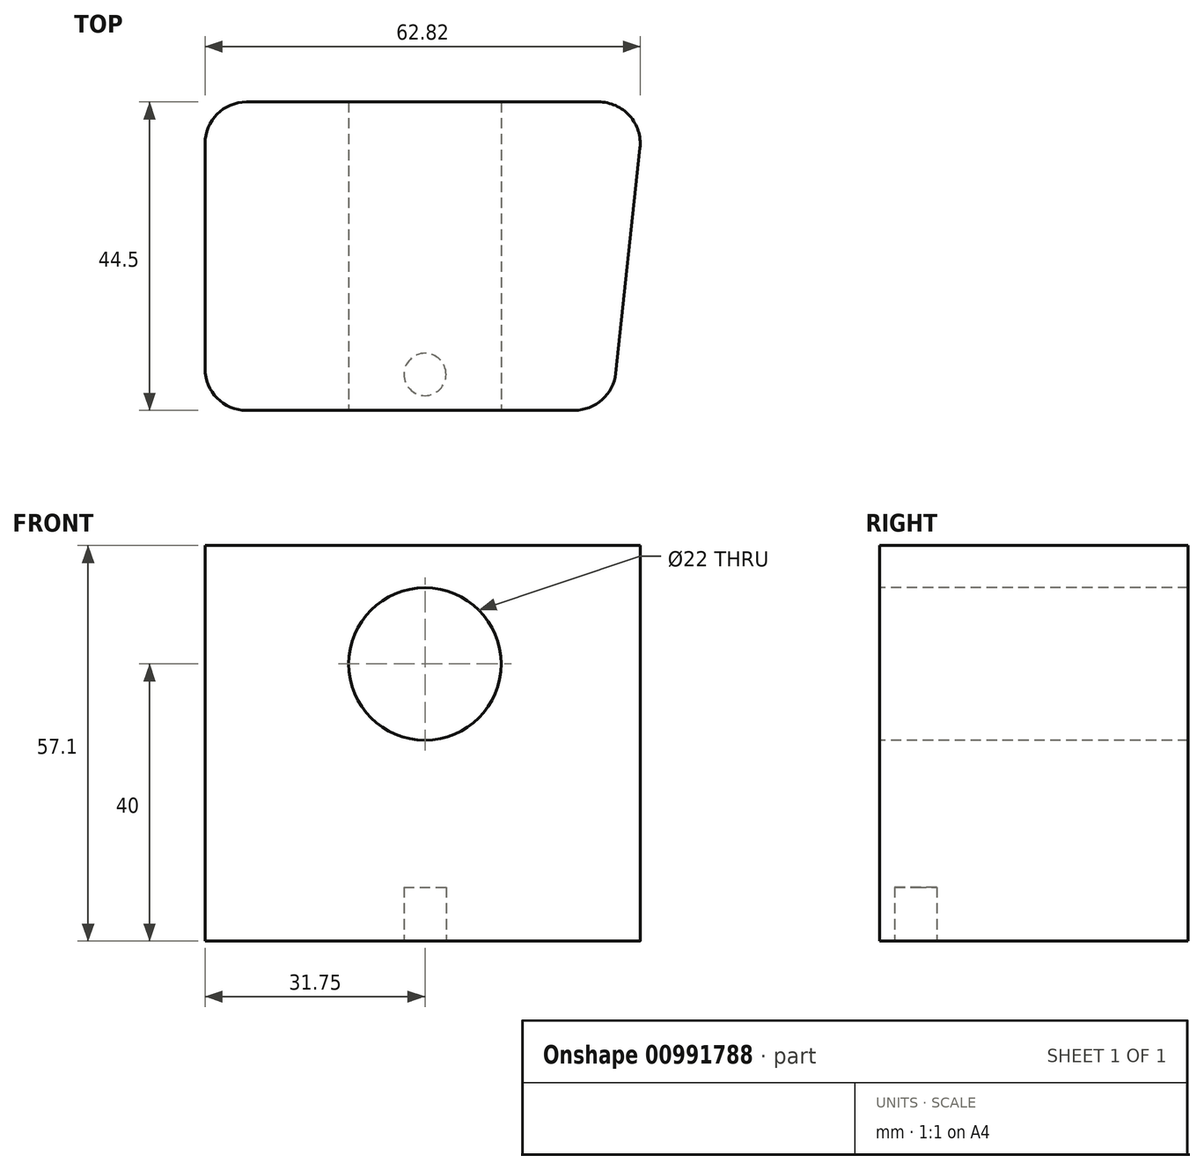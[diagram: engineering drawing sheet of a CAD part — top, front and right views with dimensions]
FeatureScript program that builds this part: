
annotation { "Feature Type Name" : "Feature", "Feature Type Description" : "" }
export const myFeature = defineFeature(function(context is Context, id is Id, definition is map)
    precondition{}
    {
        {
            var Q0;
            Q0=qCreatedBy(makeId("Top.planeOp"),FACE);
            var sketch = newSketch(context, id + "F0", { "sketchPlane" : qUnion([Q0])});
            skLineSegment(sketch, "E0.bottom", {"start": v(-31.75, 0) * mm, "end": v(26.95, 0) * mm});
            skLineSegment(sketch, "E0.top", {"start": v(-31.75, 44.5) * mm, "end": v(31.75, 44.5) * mm});
            skLineSegment(sketch, "E0.left", {"start": v(-31.75, 0) * mm, "end": v(-31.75, 44.5) * mm});
            skLineSegment(sketch, "E0.right", {"start": v(26.95, 0) * mm, "end": v(31.75, 44.5) * mm});
            skPoint(sketch, "E1", {"position": v(0, 44.5) * mm});
            skSolve(sketch);
        }
        {
            var Q0;
            Q0=makeQuery(id+"F0.imprint","IMPRINT",FACE,{"disambiguationData":[TD([[makeQuery(id+"F0.imprint","IMPRINT",EDGE,{"derivedFrom":sQuery(id+"F0.wireOp",EDGE,"E0.bottom")}),1.0]])]});
            extrude(context, id + "F1", {"entities" : qUnion([Q0]), "depth" : 57.1 * mm, "offsetDistance" : 25 * mm});
        }
        {
            var Q0;
            Q0=makeQuery(id+"F1.opExtrude","SWEPT_FACE",FACE,{"disambiguationData":[OSD([sQuery(id+"F0.wireOp",EDGE,"E0.bottom")])]});
            var sketch = newSketch(context, id + "F2", { "sketchPlane" : qUnion([Q0])});
            skCircle(sketch, "E2", {"center": v(0, 40) * mm, "radius": 11 * mm});
            skSolve(sketch);
        }
        {
            var Q0;
            Q0=makeQuery(id+"F2.imprint","IMPRINT",FACE,{"disambiguationData":[TD([[makeQuery(id+"F2.imprint","IMPRINT",EDGE,{"derivedFrom":sQuery(id+"F2.wireOp",EDGE,"E2")}),1.0]])]});
            var Q1;
            Q1=sQuery(id+"F2.wireOp",EDGE,"E2");
            extrude(context, id + "F3", {"entities" : qUnion([Q0]), "operationType" : NewBodyOperationType.REMOVE, "surfaceEntities" : qUnion([Q1]), "endBound" : BoundingType.UP_TO_NEXT, "oppositeDirection" : true, "depth" : 35.3 * mm, "offsetDistance" : 25 * mm});
        }
        {
            var Q0;
            Q0=makeQuery(id+"F1.opExtrude","CAP_FACE",FACE,{"disambiguationData":[OSD([sQuery(id+"F0.wireOp",EDGE,"E0.bottom"),sQuery(id+"F0.wireOp",EDGE,"E0.top"),sQuery(id+"F0.wireOp",EDGE,"E0.left"),sQuery(id+"F0.wireOp",EDGE,"E0.right")])],"isStart":true});
            var sketch = newSketch(context, id + "F4", { "sketchPlane" : qUnion([Q0])});
            skCircle(sketch, "E3", {"center": v(0, -5.18) * mm, "radius": 3.05 * mm});
            skSolve(sketch);
        }
        {
            var Q0;
            Q0=makeQuery(id+"F4.imprint","IMPRINT",FACE,{"disambiguationData":[TD([[makeQuery(id+"F4.imprint","IMPRINT",EDGE,{"derivedFrom":sQuery(id+"F4.wireOp",EDGE,"E3")}),1.0]])]});
            extrude(context, id + "F5", {"entities" : qUnion([Q0]), "operationType" : NewBodyOperationType.REMOVE, "oppositeDirection" : true, "depth" : 7.8 * mm, "offsetDistance" : 25 * mm});
        }
        {
            var Q0;
            Q0=makeQuery(id+"F1.opExtrude","SWEPT_EDGE",EDGE,{"disambiguationData":[OSD([sQuery(id+"F0.wireOp",EDGE,"E0.bottom"),sQuery(id+"F0.wireOp",EDGE,"E0.left")])]});
            var Q1;
            Q1=makeQuery(id+"F1.opExtrude","SWEPT_EDGE",EDGE,{"disambiguationData":[OSD([sQuery(id+"F0.wireOp",EDGE,"E0.top"),sQuery(id+"F0.wireOp",EDGE,"E0.left")])]});
            var Q2;
            Q2=makeQuery(id+"F1.opExtrude","SWEPT_EDGE",EDGE,{"disambiguationData":[OSD([sQuery(id+"F0.wireOp",EDGE,"E0.bottom"),sQuery(id+"F0.wireOp",EDGE,"E0.right")])]});
            var Q3;
            Q3=makeQuery(id+"F1.opExtrude","SWEPT_EDGE",EDGE,{"disambiguationData":[OSD([sQuery(id+"F0.wireOp",EDGE,"E0.top"),sQuery(id+"F0.wireOp",EDGE,"E0.right")])]});
            fillet(context, id + "F6", {"entities" : qUnion([Q0, Q1, Q2, Q3]), "radius" : 6 * mm, "tangentPropagation" : true, "allowEdgeOverflow" : false});
        }
    });
